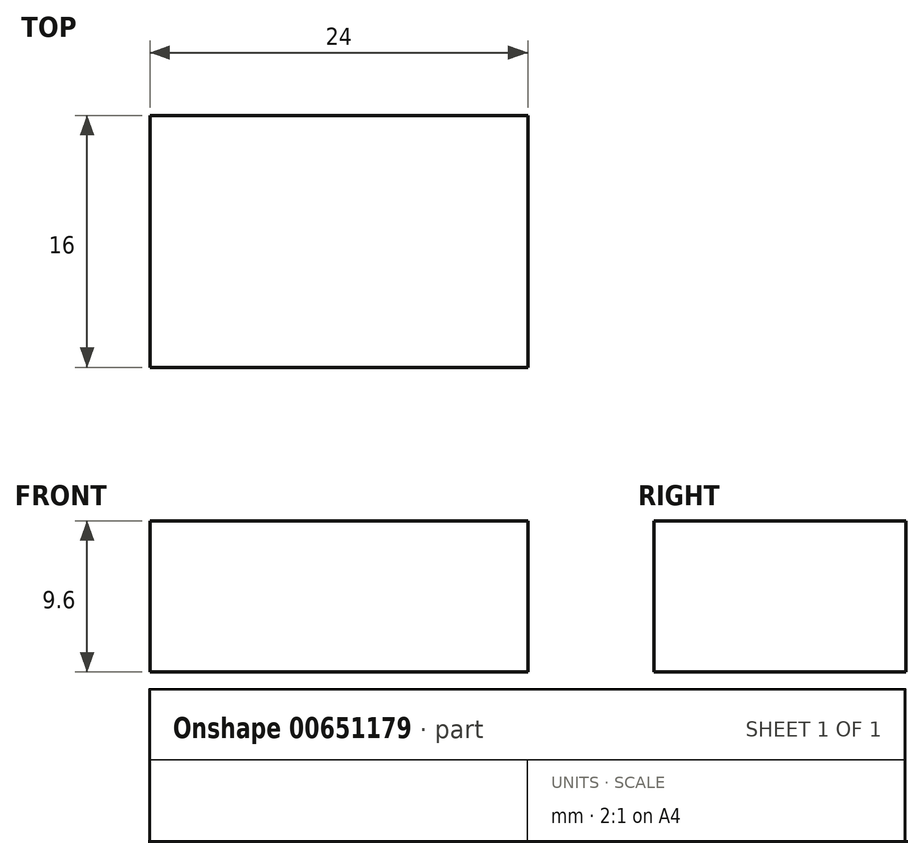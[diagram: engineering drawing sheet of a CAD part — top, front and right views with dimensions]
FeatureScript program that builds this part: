
annotation { "Feature Type Name" : "Feature", "Feature Type Description" : "" }
export const myFeature = defineFeature(function(context is Context, id is Id, definition is map)
    precondition{}
    {
        {
            var Q0;
            Q0=qCreatedBy(makeId("Top.planeOp"),FACE);
            var sketch = newSketch(context, id + "F0", { "sketchPlane" : qUnion([Q0])});
            skLineSegment(sketch, "E0.bottom", {"start": v(0, 0) * mm, "end": v(-24, 0) * mm});
            skLineSegment(sketch, "E0.top", {"start": v(0, 16) * mm, "end": v(-24, 16) * mm});
            skLineSegment(sketch, "E0.left", {"start": v(0, 0) * mm, "end": v(0, 16) * mm});
            skLineSegment(sketch, "E0.right", {"start": v(-24, 0) * mm, "end": v(-24, 16) * mm});
            skSolve(sketch);
        }
        {
            var Q0;
            Q0=makeQuery(id+"F0.imprint","IMPRINT",FACE,{"disambiguationData":[TD([[makeQuery(id+"F0.imprint","IMPRINT",EDGE,{"derivedFrom":sQuery(id+"F0.wireOp",EDGE,"E0.bottom")}),-1.0]])]});
            extrude(context, id + "F1", {"entities" : qUnion([Q0]), "depth" : 9.6 * mm, "offsetDistance" : 25.4 * mm});
        }
    });
